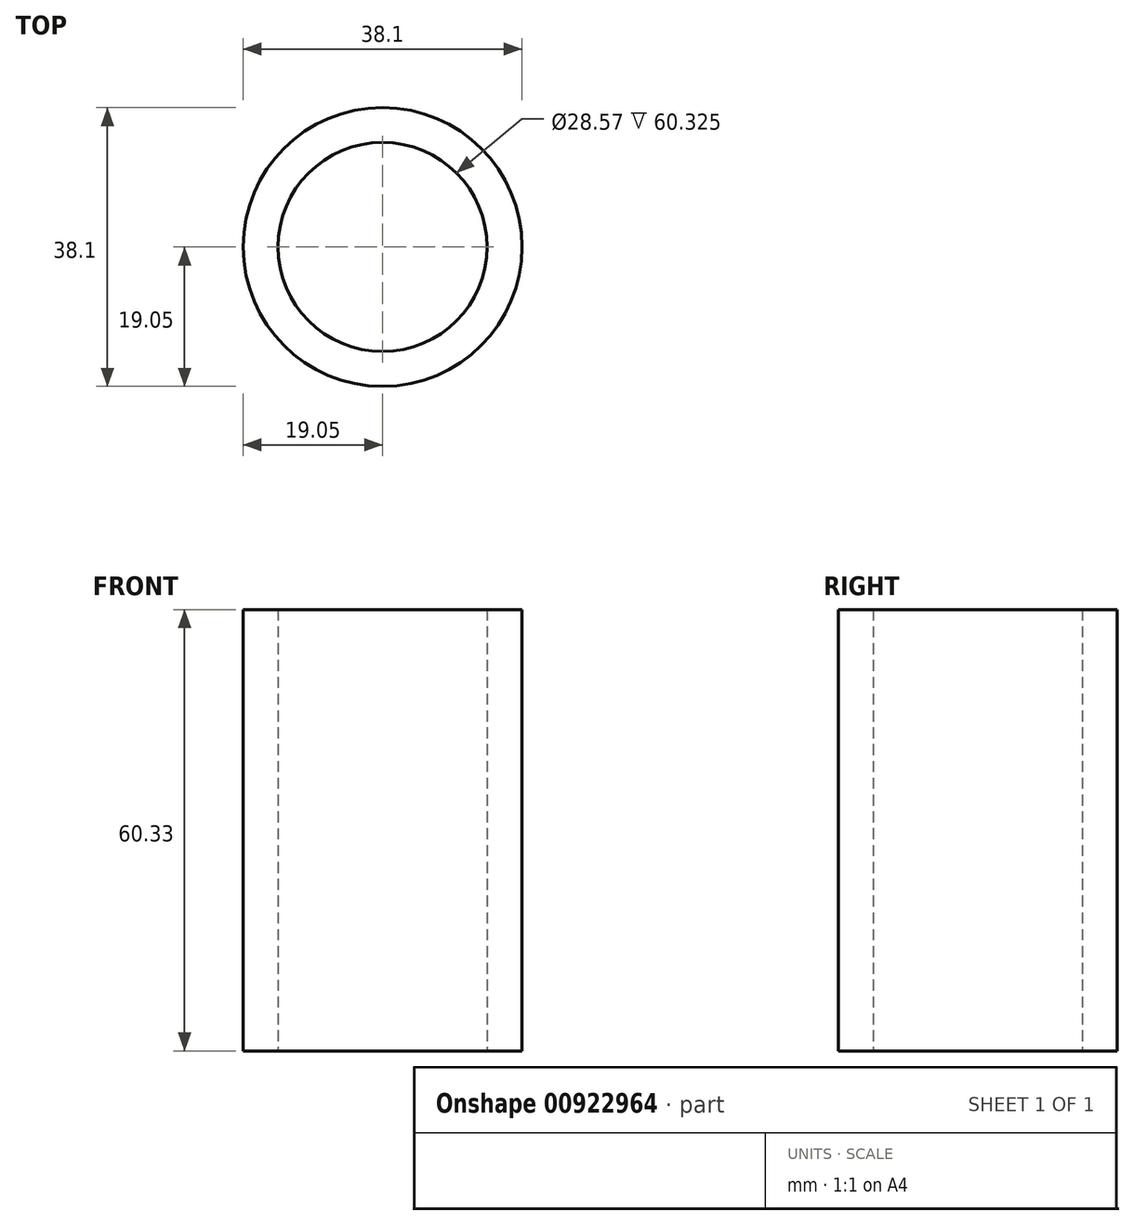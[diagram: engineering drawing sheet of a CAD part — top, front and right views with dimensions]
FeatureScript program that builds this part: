
annotation { "Feature Type Name" : "Feature", "Feature Type Description" : "" }
export const myFeature = defineFeature(function(context is Context, id is Id, definition is map)
    precondition{}
    {
        {
            var Q0;
            Q0=qCreatedBy(makeId("Front.planeOp"),FACE);
            var sketch = newSketch(context, id + "F0", { "sketchPlane" : qUnion([Q0])});
            skLineSegment(sketch, "E0", {"start": v(0, 0) * mm, "end": v(0, 42.53) * mm, "construction": true});
            skLineSegment(sketch, "E1.bottom", {"start": v(-19.05, 0) * mm, "end": v(-14.29, 0) * mm});
            skLineSegment(sketch, "E1.top", {"start": v(-19.05, 60.33) * mm, "end": v(-14.29, 60.33) * mm});
            skLineSegment(sketch, "E1.left", {"start": v(-19.05, 0) * mm, "end": v(-19.05, 60.33) * mm});
            skLineSegment(sketch, "E1.right", {"start": v(-14.29, 0) * mm, "end": v(-14.29, 60.33) * mm});
            skSolve(sketch);
        }
        {
            var Q0;
            Q0 = qSketchRegion(id + "F0", true);
            var Q1;
            Q1=sQuery(id+"F0.wireOp",EDGE,"E0");
            revolve(context, id + "F1", {"surfaceOperationType" : NewSurfaceOperationType.NEW, "entities" : qUnion([Q0]), "axis" : qUnion([Q1]), "revolveType" : RevolveType.FULL});
        }
    });
